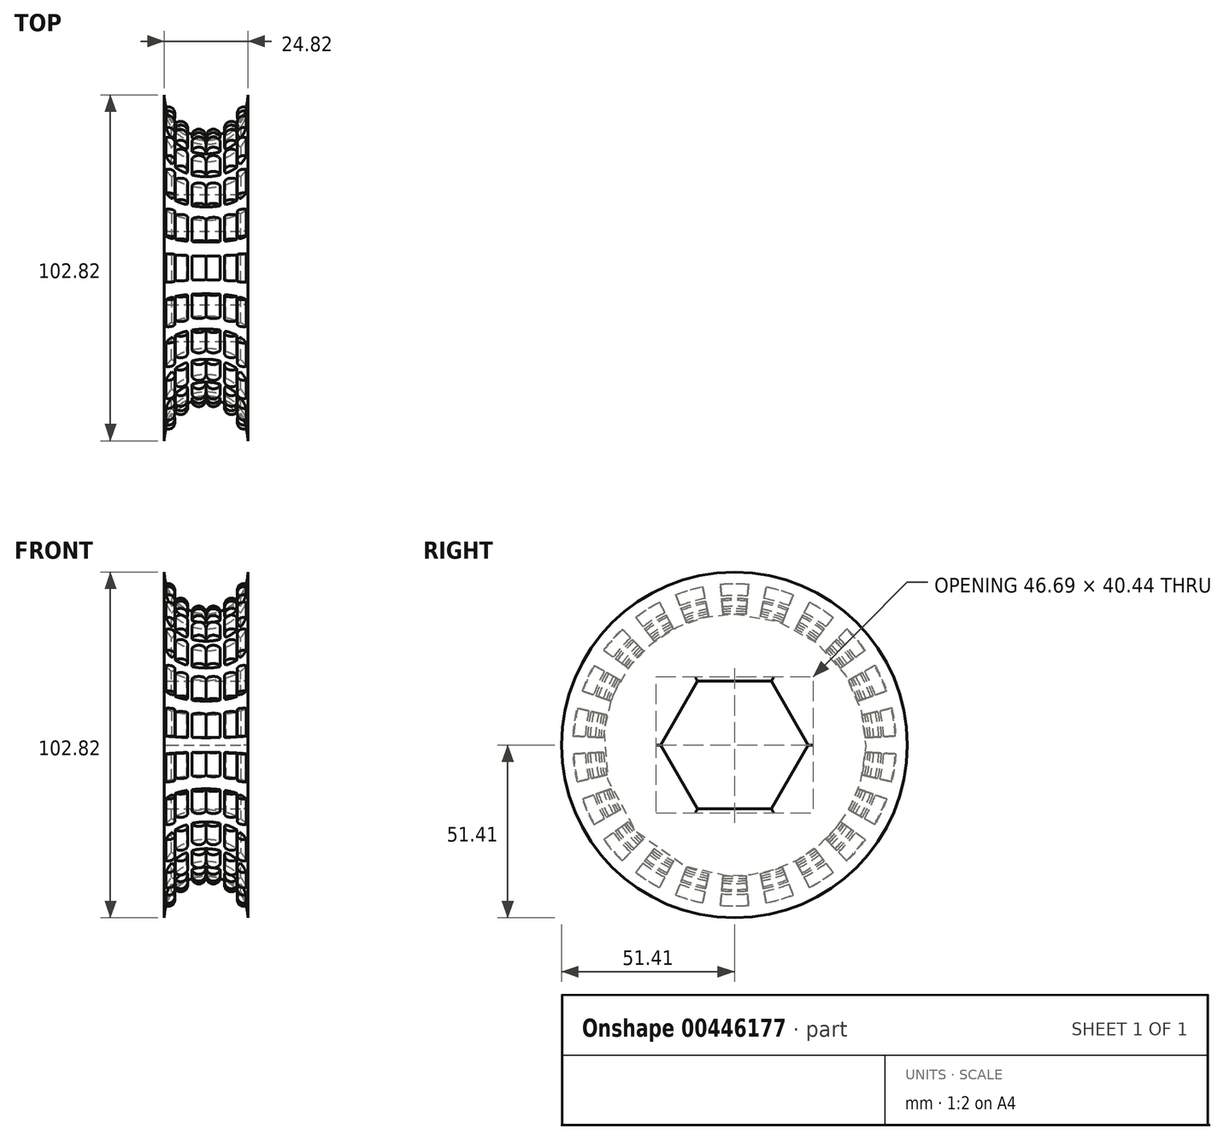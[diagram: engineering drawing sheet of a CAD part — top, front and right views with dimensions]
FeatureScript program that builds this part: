
annotation { "Feature Type Name" : "Feature", "Feature Type Description" : "" }
export const myFeature = defineFeature(function(context is Context, id is Id, definition is map)
    precondition{}
    {
        {
            var Q0;
            Q0=qCreatedBy(makeId("Front.planeOp"),FACE);
            var sketch = newSketch(context, id + "F0", { "sketchPlane" : qUnion([Q0])});
            skPoint(sketch, "E0.middle", {"position": v(0, 0) * mm});
            skArc(sketch, "E1", {"start": v(-12.41, 51.4) * mm, "mid": v(0, 39) * mm, "end": v(12.41, 51.4) * mm});
            skArc(sketch, "E2", {"start": v(-10.26, 44.42) * mm, "mid": v(-9.49, 46.9) * mm, "end": v(-11.9, 47.86) * mm});
            skArc(sketch, "E3.MirrorCS", {"start": v(10.26, 44.42) * mm, "mid": v(9.49, 46.9) * mm, "end": v(11.9, 47.86) * mm});
            skArc(sketch, "E4", {"start": v(-5.8, 40.44) * mm, "mid": v(-6.3, 43.22) * mm, "end": v(-9.1, 42.97) * mm});
            skArc(sketch, "E5", {"start": v(-0.06, 39) * mm, "mid": v(-1.8, 41.28) * mm, "end": v(-4.23, 39.74) * mm});
            skArc(sketch, "E6.MirrorCS", {"start": v(0.06, 39) * mm, "mid": v(1.8, 41.28) * mm, "end": v(4.23, 39.74) * mm});
            skArc(sketch, "E7.MirrorCS", {"start": v(5.8, 40.44) * mm, "mid": v(6.3, 43.22) * mm, "end": v(9.1, 42.97) * mm});
            skPoint(sketch, "E8.end.orphan", {"position": v(-12.41, -51.4) * mm});
            skPoint(sketch, "E8.start.orphan", {"position": v(12.41, -51.4) * mm});
            skSolve(sketch);
        }
        {
            var Q0;
            Q0=qCreatedBy(makeId("Top.planeOp"),FACE);
            var sketch = newSketch(context, id + "F1", { "sketchPlane" : qUnion([Q0])});
            skLineSegment(sketch, "E9.left", {"start": v(-12.41, 51.4) * mm, "end": v(-12.41, 0) * mm});
            skLineSegment(sketch, "E9.right", {"start": v(12.41, 51.4) * mm, "end": v(12.41, 0) * mm});
            skPoint(sketch, "E9.middle", {"position": v(0, 0) * mm});
            skArc(sketch, "E10", {"start": v(-12.41, 51.4) * mm, "mid": v(0, 39) * mm, "end": v(12.41, 51.4) * mm});
            skLineSegment(sketch, "E11", {"start": v(-12.41, 0) * mm, "end": v(12.41, 0) * mm});
            skPoint(sketch, "E12.end.orphan", {"position": v(-12.41, -51.4) * mm});
            skPoint(sketch, "E12.start.orphan", {"position": v(12.41, -51.4) * mm});
            skSolve(sketch);
        }
        {
            var Q0;
            Q0=qCreatedBy(makeId("Front.planeOp"),FACE);
            var sketch = newSketch(context, id + "F2", { "sketchPlane" : qUnion([Q0])});
            skLineSegment(sketch, "E13", {"start": v(-12.68, 0) * mm, "end": v(12.95, 0) * mm});
            skSolve(sketch);
        }
        {
            var Q0;
            Q0=makeQuery(id+"F1.imprint","IMPRINT",FACE,{"disambiguationData":[TD([[makeQuery(id+"F1.imprint","IMPRINT",EDGE,{"derivedFrom":sQuery(id+"F1.wireOp",EDGE,"E9.left")}),1.0]])]});
            var Q1;
            Q1=sQuery(id+"F1.wireOp",EDGE,"E11");
            revolve(context, id + "F3", {"entities" : qUnion([Q0]), "axis" : qUnion([Q1]), "revolveType" : RevolveType.FULL});
        }
        {
            var Q0;
            Q0 = qSketchRegion(id + "F0", true);
            var Q1;
            Q1=sQuery(id+"F2.wireOp",EDGE,"E13");
            revolve(context, id + "F4", {"entities" : qUnion([Q0]), "axis" : qUnion([Q1]), "revolveType" : RevolveType.SYMMETRIC, "angle" : 10 * degree});
        }
        {
            var Q0;
            Q0=makeQuery(id+"F4.opRevolve","SWEPT_BODY",BODY,{"disambiguationData":[OSD([sQuery(id+"F0.wireOp",EDGE,"E1"),sQuery(id+"F0.wireOp",EDGE,"E3.MirrorCS")])]});
            var Q1;
            Q1=sQuery(id+"F2.wireOp",EDGE,"E13");
            circularPattern(context, id + "F5", {"entities" : qUnion([Q0]), "axis" : qUnion([Q1]), "angle" : 360 * degree, "instanceCount" : 22, "equalSpace" : true});
        }
        {
            var Q0;
            Q0=makeQuery(id+"F4.opRevolve","SWEPT_BODY",BODY,{"disambiguationData":[OSD([sQuery(id+"F0.wireOp",EDGE,"E1"),sQuery(id+"F0.wireOp",EDGE,"E7.MirrorCS")])]});
            var Q1;
            Q1=sQuery(id+"F2.wireOp",EDGE,"E13");
            circularPattern(context, id + "F6", {"entities" : qUnion([Q0]), "axis" : qUnion([Q1]), "angle" : 360 * degree, "instanceCount" : 22, "equalSpace" : true});
        }
        {
            var Q0;
            Q0=makeQuery(id+"F4.opRevolve","SWEPT_BODY",BODY,{"disambiguationData":[OSD([sQuery(id+"F0.wireOp",EDGE,"E1"),sQuery(id+"F0.wireOp",EDGE,"E6.MirrorCS")])]});
            var Q1;
            Q1=sQuery(id+"F2.wireOp",EDGE,"E13");
            circularPattern(context, id + "F7", {"entities" : qUnion([Q0]), "axis" : qUnion([Q1]), "angle" : 360 * degree, "instanceCount" : 22, "equalSpace" : true});
        }
        {
            var Q0;
            Q0=makeQuery(id+"F4.opRevolve","SWEPT_BODY",BODY,{"disambiguationData":[OSD([sQuery(id+"F0.wireOp",EDGE,"E1"),sQuery(id+"F0.wireOp",EDGE,"E5")])]});
            var Q1;
            Q1=sQuery(id+"F2.wireOp",EDGE,"E13");
            circularPattern(context, id + "F8", {"entities" : qUnion([Q0]), "axis" : qUnion([Q1]), "angle" : 360 * degree, "instanceCount" : 22, "equalSpace" : true});
        }
        {
            var Q0;
            Q0=makeQuery(id+"F4.opRevolve","SWEPT_BODY",BODY,{"disambiguationData":[OSD([sQuery(id+"F0.wireOp",EDGE,"E1"),sQuery(id+"F0.wireOp",EDGE,"E4")])]});
            var Q1;
            Q1=sQuery(id+"F2.wireOp",EDGE,"E13");
            circularPattern(context, id + "F9", {"entities" : qUnion([Q0]), "axis" : qUnion([Q1]), "angle" : 360 * degree, "instanceCount" : 22, "equalSpace" : true});
        }
        {
            var Q0;
            Q0=makeQuery(id+"F4.opRevolve","SWEPT_BODY",BODY,{"disambiguationData":[OSD([sQuery(id+"F0.wireOp",EDGE,"E1"),sQuery(id+"F0.wireOp",EDGE,"E2")])]});
            var Q1;
            Q1=sQuery(id+"F2.wireOp",EDGE,"E13");
            circularPattern(context, id + "F10", {"entities" : qUnion([Q0]), "axis" : qUnion([Q1]), "angle" : 360 * degree, "instanceCount" : 22, "equalSpace" : true});
        }
        {
            var Q0;
            Q0=qCreatedBy(makeId("Right.planeOp"),FACE);
            var sketch = newSketch(context, id + "F11", { "sketchPlane" : qUnion([Q0])});
            skCircle(sketch, "E14.cCircle", {"center": v(0, 0) * mm, "radius": 18.95 * mm, "construction": true});
            skLineSegment(sketch, "E14.0", {"start": v(-10.94, 18.95) * mm, "end": v(10.94, 18.95) * mm});
            skLineSegment(sketch, "E14.1", {"start": v(10.94, 18.95) * mm, "end": v(21.88, 0) * mm});
            skLineSegment(sketch, "E14.2", {"start": v(21.88, 0) * mm, "end": v(10.94, -18.95) * mm});
            skLineSegment(sketch, "E14.3", {"start": v(10.94, -18.95) * mm, "end": v(-10.94, -18.95) * mm});
            skLineSegment(sketch, "E14.4", {"start": v(-10.94, -18.95) * mm, "end": v(-21.88, 0) * mm});
            skLineSegment(sketch, "E14.5", {"start": v(-21.88, 0) * mm, "end": v(-10.94, 18.95) * mm});
            skPoint(sketch, "E14.0.midPoint", {"position": v(0, 18.95) * mm});
            skSolve(sketch);
        }
        {
            var Q0;
            Q0 = qSketchRegion(id + "F11", true);
            extrude(context, id + "F12", {"entities" : qUnion([Q0]), "operationType" : NewBodyOperationType.REMOVE, "endBound" : BoundingType.SYMMETRIC, "oppositeDirection" : true, "depth" : 25.4 * mm});
        }
        {
            var Q0;
            Q0=makeQuery(id+"F12.boolean.opBoolean","INTERSECT",EDGE,{"derivedFrom":[makeQuery(id+"F3.opRevolve","SWEPT_FACE",FACE,{"disambiguationData":[OSD([sQuery(id+"F1.wireOp",EDGE,"E9.left")])]}),makeQuery(id+"F12.opExtrude","SWEPT_FACE",FACE,{"disambiguationData":[OSD([sQuery(id+"F11.wireOp",EDGE,"E14.4")])]})]});
            var Q1;
            Q1=makeQuery(id+"F12.boolean.opBoolean","INTERSECT",EDGE,{"derivedFrom":[makeQuery(id+"F3.opRevolve","SWEPT_FACE",FACE,{"disambiguationData":[OSD([sQuery(id+"F1.wireOp",EDGE,"E9.left")])]}),makeQuery(id+"F12.opExtrude","SWEPT_FACE",FACE,{"disambiguationData":[OSD([sQuery(id+"F11.wireOp",EDGE,"E14.2")])]})]});
            var Q2;
            Q2=makeQuery(id+"F12.boolean.opBoolean","INTERSECT",EDGE,{"derivedFrom":[makeQuery(id+"F3.opRevolve","SWEPT_FACE",FACE,{"disambiguationData":[OSD([sQuery(id+"F1.wireOp",EDGE,"E9.right")])]}),makeQuery(id+"F12.opExtrude","SWEPT_FACE",FACE,{"disambiguationData":[OSD([sQuery(id+"F11.wireOp",EDGE,"E14.4")])]})]});
            var Q3;
            Q3=makeQuery(id+"F12.boolean.opBoolean","INTERSECT",EDGE,{"derivedFrom":[makeQuery(id+"F3.opRevolve","SWEPT_FACE",FACE,{"disambiguationData":[OSD([sQuery(id+"F1.wireOp",EDGE,"E9.left")])]}),makeQuery(id+"F12.opExtrude","SWEPT_FACE",FACE,{"disambiguationData":[OSD([sQuery(id+"F11.wireOp",EDGE,"E14.5")])]})]});
            var Q4;
            Q4=makeQuery(id+"F12.boolean.opBoolean","INTERSECT",EDGE,{"derivedFrom":[makeQuery(id+"F3.opRevolve","SWEPT_FACE",FACE,{"disambiguationData":[OSD([sQuery(id+"F1.wireOp",EDGE,"E9.right")])]}),makeQuery(id+"F12.opExtrude","SWEPT_FACE",FACE,{"disambiguationData":[OSD([sQuery(id+"F11.wireOp",EDGE,"E14.3")])]})]});
            var Q5;
            Q5=makeQuery(id+"F12.boolean.opBoolean","INTERSECT",EDGE,{"derivedFrom":[makeQuery(id+"F3.opRevolve","SWEPT_FACE",FACE,{"disambiguationData":[OSD([sQuery(id+"F1.wireOp",EDGE,"E9.right")])]}),makeQuery(id+"F12.opExtrude","SWEPT_FACE",FACE,{"disambiguationData":[OSD([sQuery(id+"F11.wireOp",EDGE,"E14.2")])]})]});
            var Q6;
            Q6=makeQuery(id+"F12.boolean.opBoolean","INTERSECT",EDGE,{"derivedFrom":[makeQuery(id+"F3.opRevolve","SWEPT_FACE",FACE,{"disambiguationData":[OSD([sQuery(id+"F1.wireOp",EDGE,"E9.right")])]}),makeQuery(id+"F12.opExtrude","SWEPT_FACE",FACE,{"disambiguationData":[OSD([sQuery(id+"F11.wireOp",EDGE,"E14.0")])]})]});
            var Q7;
            Q7=makeQuery(id+"F12.boolean.opBoolean","INTERSECT",EDGE,{"derivedFrom":[makeQuery(id+"F3.opRevolve","SWEPT_FACE",FACE,{"disambiguationData":[OSD([sQuery(id+"F1.wireOp",EDGE,"E9.right")])]}),makeQuery(id+"F12.opExtrude","SWEPT_FACE",FACE,{"disambiguationData":[OSD([sQuery(id+"F11.wireOp",EDGE,"E14.1")])]})]});
            var Q8;
            Q8=makeQuery(id+"F12.boolean.opBoolean","INTERSECT",EDGE,{"derivedFrom":[makeQuery(id+"F3.opRevolve","SWEPT_FACE",FACE,{"disambiguationData":[OSD([sQuery(id+"F1.wireOp",EDGE,"E9.left")])]}),makeQuery(id+"F12.opExtrude","SWEPT_FACE",FACE,{"disambiguationData":[OSD([sQuery(id+"F11.wireOp",EDGE,"E14.0")])]})]});
            var Q9;
            Q9=makeQuery(id+"F12.boolean.opBoolean","INTERSECT",EDGE,{"derivedFrom":[makeQuery(id+"F3.opRevolve","SWEPT_FACE",FACE,{"disambiguationData":[OSD([sQuery(id+"F1.wireOp",EDGE,"E9.left")])]}),makeQuery(id+"F12.opExtrude","SWEPT_FACE",FACE,{"disambiguationData":[OSD([sQuery(id+"F11.wireOp",EDGE,"E14.3")])]})]});
            var Q10;
            Q10=makeQuery(id+"F12.boolean.opBoolean","INTERSECT",EDGE,{"derivedFrom":[makeQuery(id+"F3.opRevolve","SWEPT_FACE",FACE,{"disambiguationData":[OSD([sQuery(id+"F1.wireOp",EDGE,"E9.right")])]}),makeQuery(id+"F12.opExtrude","SWEPT_FACE",FACE,{"disambiguationData":[OSD([sQuery(id+"F11.wireOp",EDGE,"E14.5")])]})]});
            var Q11;
            Q11=makeQuery(id+"F12.boolean.opBoolean","INTERSECT",EDGE,{"derivedFrom":[makeQuery(id+"F3.opRevolve","SWEPT_FACE",FACE,{"disambiguationData":[OSD([sQuery(id+"F1.wireOp",EDGE,"E9.left")])]}),makeQuery(id+"F12.opExtrude","SWEPT_FACE",FACE,{"disambiguationData":[OSD([sQuery(id+"F11.wireOp",EDGE,"E14.1")])]})]});
            fillet(context, id + "F13", {"entities" : qUnion([Q0, Q1, Q2, Q3, Q4, Q5, Q6, Q7, Q8, Q9, Q10, Q11]), "radius" : 1.27 * mm, "tangentPropagation" : true, "allowEdgeOverflow" : false});
        }
    });
